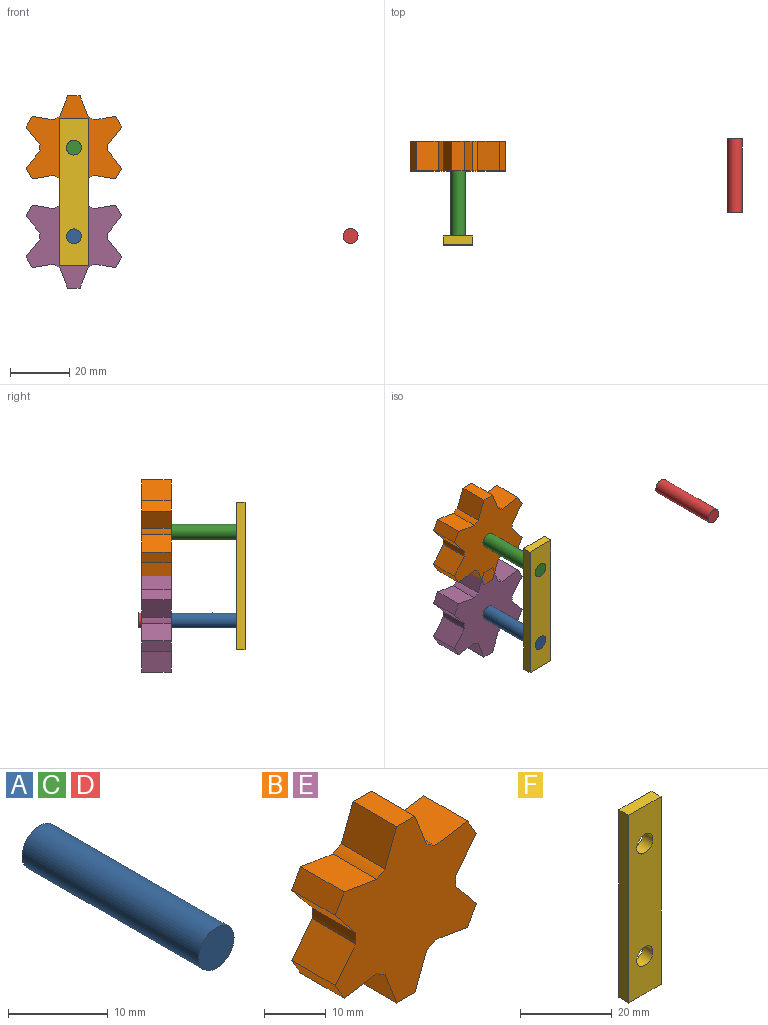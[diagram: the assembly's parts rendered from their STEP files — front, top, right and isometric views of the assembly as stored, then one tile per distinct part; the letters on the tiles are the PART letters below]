
ASSEMBLY  parts=6 mates=6
PART A: 3 faces, bbox 5x25x5 mm
  f0: cylinder r=2.5mm len=25mm, axis (0,1,0), area 392.7mm2, adj f1,f2
  f1: plane 5x5mm, normal (0,-1,0), area 19.6mm2, adj f0
  f2: plane 5x5mm, normal (0,1,0), area 19.6mm2, adj f0
PART B: 26 faces, bbox 32.4x10x35 mm
  f0: plane 10x7.44mm, normal (0.16,0,0.99), area 75.3mm2, adj f1,f23,f24,f25
  f1: plane 10x3.61mm, normal (-0.87,0,0.5), area 41.7mm2, adj f0,f2,f24,f25
  f2: plane 10x5.84mm, normal (-0.78,0,-0.63), area 75.3mm2, adj f1,f3,f24,f25
  f3: cylinder r=11.5mm len=10mm, axis (0,1,0), area 22.1mm2, adj f2,f4,f24,f25
  f4: plane 10x5.84mm, normal (-0.78,0,0.63), area 75.3mm2, adj f3,f5,f24,f25
  f5: plane 10x3.61mm, normal (-0.87,0,-0.5), area 41.7mm2, adj f4,f6,f24,f25
  f6: plane 10x7.44mm, normal (0.16,0,-0.99), area 75.3mm2, adj f5,f7,f24,f25
  f7: cylinder r=11.5mm len=10mm, axis (0,1,0), area 22.1mm2, adj f6,f8,f24,f25
  f8: plane 10x7.04mm, normal (-0.93,0,-0.36), area 75.3mm2, adj f7,f9,f24,f25
  f9: plane 10x4.17mm, normal (0,0,-1), area 41.7mm2, adj f8,f10,f24,f25
  f10: plane 10x7.04mm, normal (0.93,0,-0.36), area 75.3mm2, adj f9,f11,f24,f25
  f11: cylinder r=11.5mm len=10mm, axis (0,1,0), area 22.1mm2, adj f10,f12,f24,f25
  f12: plane 10x7.44mm, normal (-0.16,0,-0.99), area 75.3mm2, adj f11,f13,f24,f25
  f13: plane 10x3.61mm, normal (0.87,0,-0.5), area 41.7mm2, adj f12,f14,f24,f25
  f14: plane 10x5.84mm, normal (0.78,0,0.63), area 75.3mm2, adj f13,f15,f24,f25
  f15: cylinder r=11.5mm len=10mm, axis (0,1,0), area 22.1mm2, adj f14,f16,f24,f25
  f16: plane 10x5.84mm, normal (0.78,0,-0.63), area 75.3mm2, adj f15,f17,f24,f25
  f17: plane 10x3.61mm, normal (0.87,0,0.5), area 41.7mm2, adj f16,f18,f24,f25
  f18: plane 10x7.44mm, normal (-0.16,0,0.99), area 75.3mm2, adj f17,f19,f24,f25
  f19: cylinder r=11.5mm len=10mm, axis (0,1,0), area 22.1mm2, adj f18,f20,f24,f25
  f20: plane 10x7.04mm, normal (0.93,0,0.36), area 75.3mm2, adj f19,f21,f24,f25
  f21: plane 10x4.17mm, normal (0,0,1), area 41.7mm2, adj f20,f22,f24,f25
  f22: plane 10x7.04mm, normal (-0.93,0,0.36), area 75.3mm2, adj f21,f23,f24,f25
  f23: cylinder r=11.5mm len=10mm, axis (0,1,0), area 22.1mm2, adj f0,f22,f24,f25
  f24: plane 35x32.4mm, normal (0,-1,0), area 665mm2, adj f0,f1,f2,f3,f4,f5,f6,f7
  f25: plane 35x32.4mm, normal (0,1,0), area 665mm2, adj f0,f1,f2,f3,f4,f5,f6,f7
PART C: same geometry as A
PART D: same geometry as A
PART E: same geometry as B
PART F: 8 faces, bbox 10x3x50 mm
  f0: plane 10x3mm, normal (0,0,1), area 30mm2, adj f1,f5,f6,f7
  f1: plane 50x3mm, normal (-1,0,0), area 150mm2, adj f0,f2,f6,f7
  f2: plane 10x3mm, normal (0,0,-1), area 30mm2, adj f1,f5,f6,f7
  f3: cylinder r=2.5mm len=5mm, axis (0,1,0), area 47.1mm2, adj f6,f7
  f4: cylinder r=2.5mm len=5mm, axis (0,1,0), area 47.1mm2, adj f6,f7
  f5: plane 50x3mm, normal (1,0,0), area 150mm2, adj f0,f2,f6,f7
  f6: plane 50x10mm, normal (0,-1,0), area 460.7mm2, adj f0,f1,f2,f3,f4,f5
  f7: plane 50x10mm, normal (0,1,0), area 460.7mm2, adj f0,f1,f2,f3,f4,f5
PLACE A t=(-83.01,10.79,5.66)mm
PLACE B t=(-83.01,45.79,35.66)mm
PLACE C t=(-83.01,10.79,35.66)mm
PLACE D t=(10.54,21.68,5.78)mm
PLACE E t=(-83.01,45.79,5.66)mm
PLACE F t=(-83.01,1.29,35.66)mm
MATE fastened E.f3 <-> A.f0  axis (0,-1,0) through (-18.62,23.29,19.46)mm
MATE planar E.f3 <-> A.f0  axis (0,-1,0) through (-18.62,23.29,19.46)mm
MATE planar B.f3 <-> C.f0  axis (0,-1,0) through (-18.62,23.29,49.46)mm
MATE revolute A.f0 <-> F.f4  axis (0,-1,0) through (-18.62,-1.71,19.46)mm
MATE fastened B.f3 <-> C.f0  axis (0,-1,0) through (-18.62,23.29,49.46)mm
MATE revolute C.f0 <-> F.f3  axis (0,-1,0) through (-18.62,-1.71,49.46)mm
